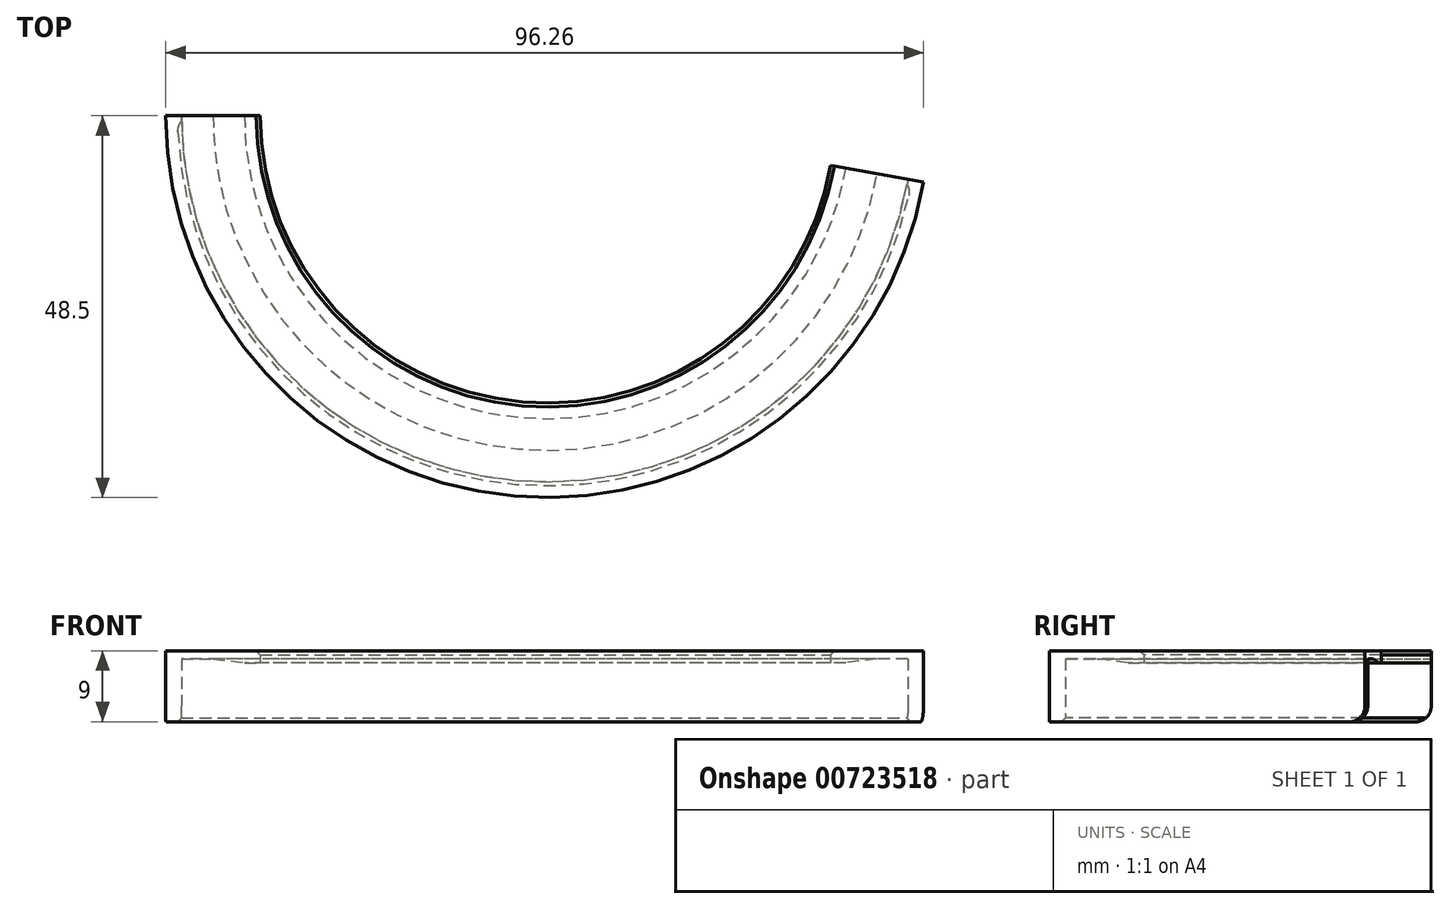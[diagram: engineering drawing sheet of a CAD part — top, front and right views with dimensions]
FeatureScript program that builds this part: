
annotation { "Feature Type Name" : "Feature", "Feature Type Description" : "" }
export const myFeature = defineFeature(function(context is Context, id is Id, definition is map)
    precondition{}
    {
        {
            var Q0;
            Q0=qCreatedBy(makeId("Front.planeOp"),FACE);
            var sketch = newSketch(context, id + "F0", { "sketchPlane" : qUnion([Q0])});
            skLineSegment(sketch, "E0", {"start": v(-48.5, 0) * mm, "end": v(-48.5, 9) * mm});
            skLineSegment(sketch, "E1", {"start": v(-48.5, 9) * mm, "end": v(-36.5, 9) * mm});
            skLineSegment(sketch, "E2", {"start": v(-46.5, 8) * mm, "end": v(-46.5, 0) * mm});
            skLineSegment(sketch, "E3", {"start": v(-48.5, 0) * mm, "end": v(-46.5, 0) * mm});
            skLineSegment(sketch, "E4", {"start": v(0, 0) * mm, "end": v(0, 8.5) * mm, "construction": true});
            skLineSegment(sketch, "E5", {"start": v(-46.5, 8) * mm, "end": v(-42.5, 8) * mm});
            skLineSegment(sketch, "E6", {"start": v(-42.5, 8) * mm, "end": v(-38.5, 7.5) * mm});
            skLineSegment(sketch, "E7", {"start": v(-38.5, 7.5) * mm, "end": v(-36.5, 7.5) * mm});
            skLineSegment(sketch, "E8", {"start": v(-36.5, 9) * mm, "end": v(-36.5, 7.5) * mm});
            skSolve(sketch);
        }
        {
            var Q0;
            Q0=makeQuery(id+"F0.imprint","IMPRINT",FACE,{"disambiguationData":[TD([[makeQuery(id+"F0.imprint","IMPRINT",EDGE,{"derivedFrom":sQuery(id+"F0.wireOp",EDGE,"E0")}),-1.0]])]});
            var Q1;
            Q1=sQuery(id+"F0.wireOp",EDGE,"E4");
            revolve(context, id + "F1", {"surfaceOperationType" : NewSurfaceOperationType.NEW, "entities" : qUnion([Q0]), "axis" : qUnion([Q1]), "revolveType" : RevolveType.ONE_DIRECTION, "angle" : 170 * degree});
        }
        {
            var Q0;
            Q0=makeQuery(id+"F1.opRevolve","SWEPT_EDGE",EDGE,{"disambiguationData":[OSD([sQuery(id+"F0.wireOp",EDGE,"E2"),sQuery(id+"F0.wireOp",EDGE,"E3")])]});
            chamfer(context, id + "F2", {"entities" : qUnion([Q0]), "width" : 0.5 * mm, "tangentPropagation" : true});
        }
        {
            var Q0;
            Q0=makeQuery(id+"F1.opRevolve","CAP_EDGE",EDGE,{"disambiguationData":[OSD([sQuery(id+"F0.wireOp",EDGE,"E3")])],"isStart":false});
            var Q1;
            Q1=makeQuery(id+"F1.opRevolve","CAP_EDGE",EDGE,{"disambiguationData":[OSD([sQuery(id+"F0.wireOp",EDGE,"E3")])],"isStart":true});
            var Q2;
            Q2=makeQuery(id+"F1.opRevolve","CAP_EDGE",EDGE,{"disambiguationData":[OSD([sQuery(id+"F0.wireOp",EDGE,"TCHEb9FH-Yg0b-P5xk-5ACr-TTJ6z789g5u8")])],"isStart":true});
            var Q3;
            Q3=makeQuery(id+"F1.opRevolve","CAP_EDGE",EDGE,{"disambiguationData":[OSD([sQuery(id+"F0.wireOp",EDGE,"TCHEb9FH-Yg0b-P5xk-5ACr-TTJ6z789g5u8")])],"isStart":false});
            fillet(context, id + "F3", {"entities" : qUnion([Q0, Q1, Q2, Q3]), "radius" : 2 * mm, "tangentPropagation" : true, "allowEdgeOverflow" : false});
        }
        {
            var Q0;
            Q0=makeQuery(id+"F1.opRevolve","SWEPT_EDGE",EDGE,{"disambiguationData":[OSD([sQuery(id+"F0.wireOp",EDGE,"E1"),sQuery(id+"F0.wireOp",EDGE,"E8")])]});
            chamfer(context, id + "F4", {"entities" : qUnion([Q0]), "width" : 0.5 * mm, "tangentPropagation" : true});
        }
    });
